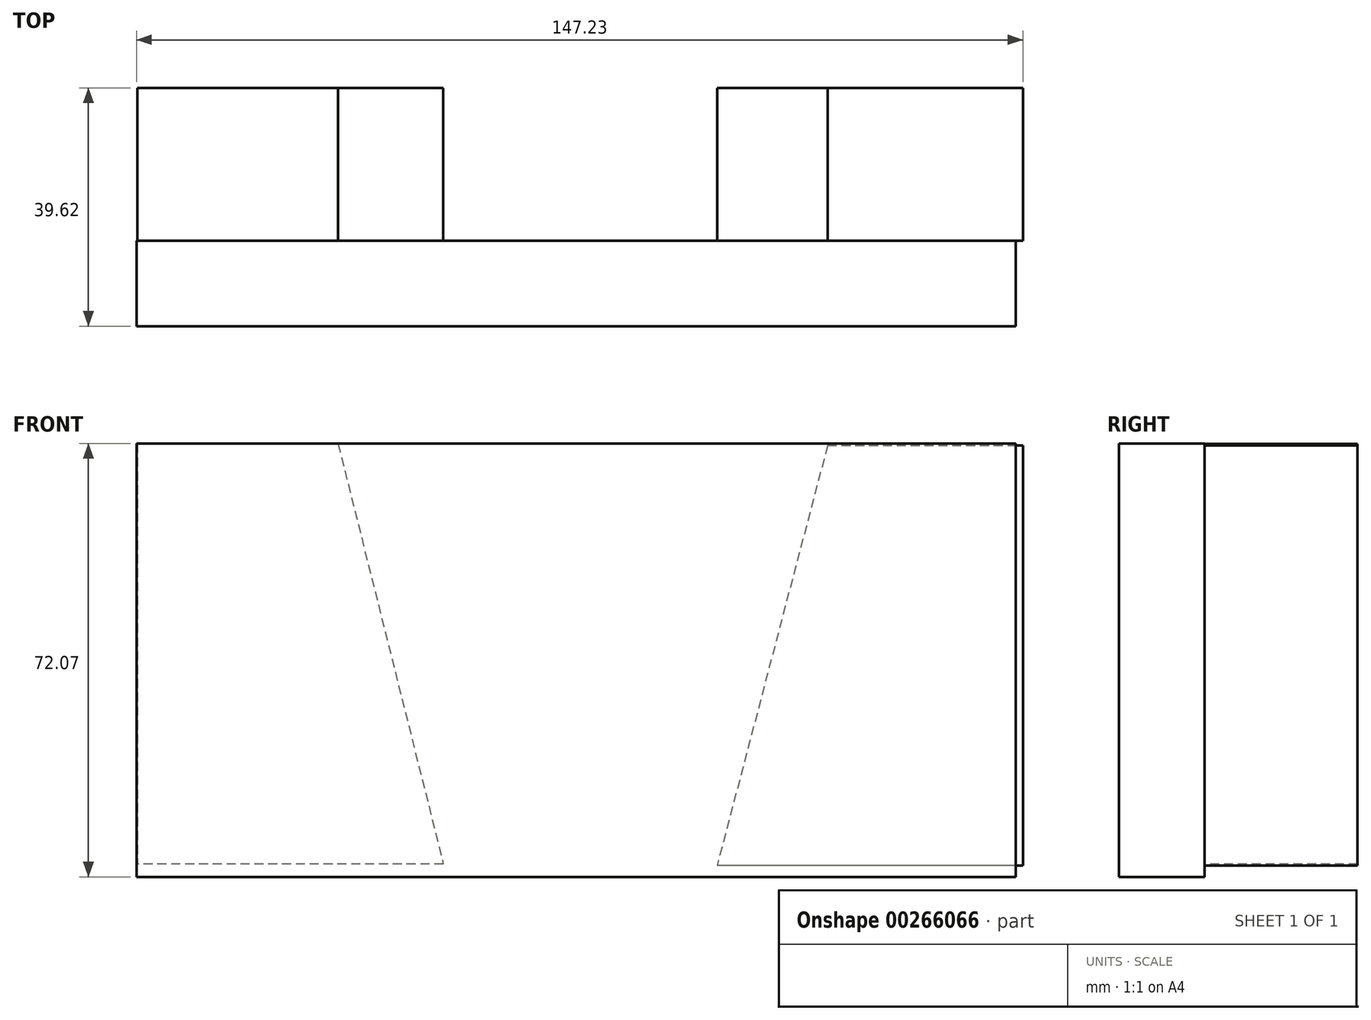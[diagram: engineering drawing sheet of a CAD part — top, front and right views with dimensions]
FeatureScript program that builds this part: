
annotation { "Feature Type Name" : "Feature", "Feature Type Description" : "" }
export const myFeature = defineFeature(function(context is Context, id is Id, definition is map)
    precondition{}
    {
        {
            var Q0;
            Q0=qCreatedBy(makeId("Front.planeOp"),FACE);
            var sketch = newSketch(context, id + "F0", { "sketchPlane" : qUnion([Q0])});
            skLineSegment(sketch, "E0.bottom", {"start": v(-73.03, 37.5) * mm, "end": v(73.03, 37.5) * mm});
            skLineSegment(sketch, "E0.left", {"start": v(-73.03, 37.5) * mm, "end": v(-73.03, -51.2) * mm});
            skLineSegment(sketch, "E0.right", {"start": v(73.03, 37.5) * mm, "end": v(73.03, -51.2) * mm});
            skLineSegment(sketch, "E1", {"start": v(-73.03, -34.56) * mm, "end": v(73.03, -34.56) * mm});
            skSolve(sketch);
        }
        {
            var Q0;
            Q0 = qSketchRegion(id + "F0", true);
            extrude(context, id + "F1", {"entities" : qUnion([Q0]), "depth" : 14.22 * mm});
        }
        {
            var Q0;
            Q0=qCreatedBy(makeId("Front.planeOp"),FACE);
            var sketch = newSketch(context, id + "F2", { "sketchPlane" : qUnion([Q0])});
            skLineSegment(sketch, "E2", {"start": v(41.76, 37.16) * mm, "end": v(23.4, -32.69) * mm});
            skLineSegment(sketch, "E3", {"start": v(-39.56, 37.45) * mm, "end": v(-22.07, -32.4) * mm});
            skLineSegment(sketch, "E4", {"start": v(41.76, 37.16) * mm, "end": v(74.2, 37.16) * mm});
            skLineSegment(sketch, "E5", {"start": v(74.2, 37.16) * mm, "end": v(74.2, -32.69) * mm});
            skLineSegment(sketch, "E6", {"start": v(74.2, -32.69) * mm, "end": v(23.4, -32.69) * mm});
            skLineSegment(sketch, "E7", {"start": v(-22.07, -32.4) * mm, "end": v(-72.87, -32.4) * mm});
            skLineSegment(sketch, "E8", {"start": v(-39.56, 37.45) * mm, "end": v(-72.87, 37.45) * mm});
            skLineSegment(sketch, "E9", {"start": v(-72.87, 37.45) * mm, "end": v(-72.87, -32.4) * mm});
            skLineSegment(sketch, "E10", {"start": v(-39.56, 37.45) * mm, "end": v(41.76, 37.16) * mm});
            skSolve(sketch);
        }
        {
            var Q0;
            Q0 = qSketchRegion(id + "F2", true);
            extrude(context, id + "F3", {"entities" : qUnion([Q0]), "oppositeDirection" : true, "depth" : 25.4 * mm});
        }
    });
